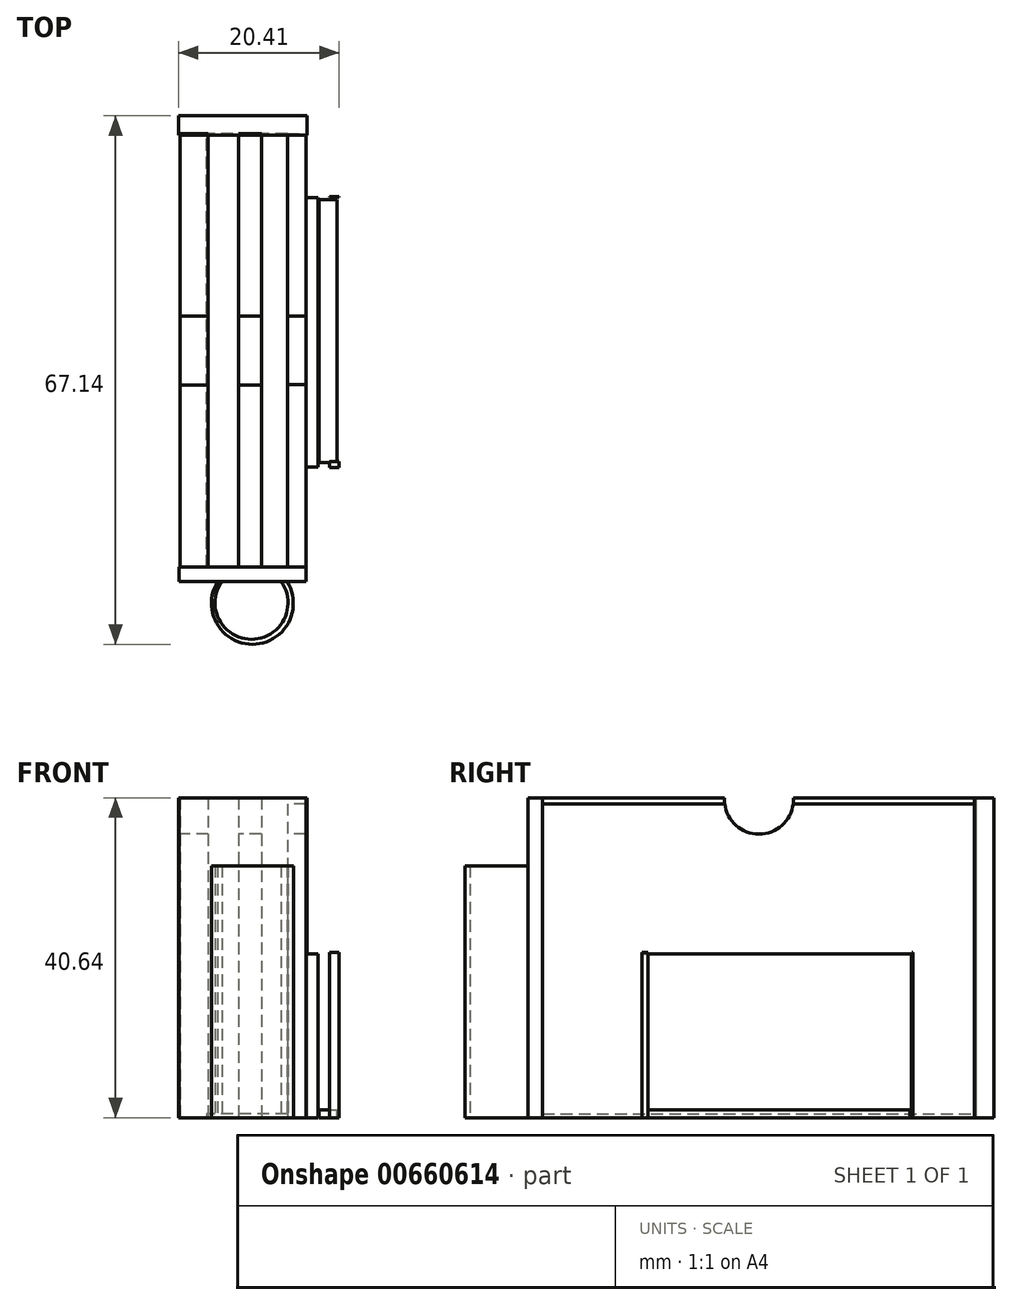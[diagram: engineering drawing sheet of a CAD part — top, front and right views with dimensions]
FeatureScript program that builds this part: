
annotation { "Feature Type Name" : "Feature", "Feature Type Description" : "" }
export const myFeature = defineFeature(function(context is Context, id is Id, definition is map)
    precondition{}
    {
        {
            var Q0;
            Q0=qCreatedBy(makeId("Top.planeOp"),FACE);
            var sketch = newSketch(context, id + "F0", { "sketchPlane" : qUnion([Q0])});
            skLineSegment(sketch, "E0.bottom", {"start": v(0, 0) * mm, "end": v(2.34, 0) * mm});
            skLineSegment(sketch, "E0.top", {"start": v(0, 55.03) * mm, "end": v(2.34, 55.03) * mm});
            skLineSegment(sketch, "E0.left", {"start": v(0, 0) * mm, "end": v(0, 55.03) * mm});
            skLineSegment(sketch, "E0.right", {"start": v(2.34, 0) * mm, "end": v(2.34, 55.03) * mm});
            skSolve(sketch);
        }
        {
            var Q0;
            Q0=makeQuery(id+"F0.imprint","IMPRINT",FACE,{"disambiguationData":[TD([[makeQuery(id+"F0.imprint","IMPRINT",EDGE,{"derivedFrom":sQuery(id+"F0.wireOp",EDGE,"E0.bottom")}),1.0]])]});
            extrude(context, id + "F1", {"entities" : qUnion([Q0]), "depth" : 39.88 * mm, "offsetDistance" : 25.4 * mm});
        }
        {
            var Q0;
            Q0=qCreatedBy(makeId("Top.planeOp"),FACE);
            var sketch = newSketch(context, id + "F2", { "sketchPlane" : qUnion([Q0])});
            skLineSegment(sketch, "E1", {"start": v(0, 0) * mm, "end": v(-3.29, 0) * mm});
            skLineSegment(sketch, "E2", {"start": v(-3.29, 0) * mm, "end": v(-3.29, 55.03) * mm});
            skLineSegment(sketch, "E3", {"start": v(-3.29, 55.03) * mm, "end": v(0, 55.03) * mm});
            skLineSegment(sketch, "E4", {"start": v(0, 55.03) * mm, "end": v(-6.23, 55.03) * mm});
            skLineSegment(sketch, "E5", {"start": v(-6.23, 55.03) * mm, "end": v(-6.23, 0) * mm});
            skLineSegment(sketch, "E6", {"start": v(-6.23, 0) * mm, "end": v(-3.29, 0) * mm});
            skLineSegment(sketch, "E7", {"start": v(-10.05, 0) * mm, "end": v(-10.05, 55.03) * mm});
            skLineSegment(sketch, "E8", {"start": v(-10.05, 55.03) * mm, "end": v(-6.23, 55.03) * mm});
            skLineSegment(sketch, "E9", {"start": v(-10.05, 0) * mm, "end": v(-6.23, 0) * mm});
            skLineSegment(sketch, "E10", {"start": v(-10.05, 55.03) * mm, "end": v(-13.63, 55.03) * mm});
            skLineSegment(sketch, "E11", {"start": v(-13.63, 55.03) * mm, "end": v(-13.63, 0) * mm});
            skLineSegment(sketch, "E12", {"start": v(-13.63, 0) * mm, "end": v(-10.05, 0) * mm});
            skSolve(sketch);
        }
        {
            var Q0;
            {var subQ0=sQuery(id+"F2.wireOp",EDGE,"E2");Q0=makeQuery(id+"F2.imprint","IMPRINT",FACE,{"disambiguationData":[TD([[makeQuery(id+"F2.imprint","IMPRINT",EDGE,{"derivedFrom":subQ0}),1.0]])]});}
            var Q1;
            Q1=makeQuery(id+"F2.imprint","IMPRINT",FACE,{"disambiguationData":[TD([[makeQuery(id+"F2.imprint","IMPRINT",EDGE,{"derivedFrom":sQuery(id+"F2.wireOp",EDGE,"E7")}),1.0]])]});
            extrude(context, id + "F3", {"entities" : qUnion([Q0, Q1]), "depth" : 40.64 * mm, "offsetDistance" : 25.4 * mm});
        }
        {
            var Q0;
            Q0=qCreatedBy(makeId("Top.planeOp"),FACE);
            var sketch = newSketch(context, id + "F4", { "sketchPlane" : qUnion([Q0])});
            skLineSegment(sketch, "E13", {"start": v(-13.78, 0) * mm, "end": v(2.4, 0) * mm});
            skLineSegment(sketch, "E14", {"start": v(2.4, 0) * mm, "end": v(2.4, -1.87) * mm});
            skLineSegment(sketch, "E15", {"start": v(2.4, -1.87) * mm, "end": v(-13.78, -1.87) * mm});
            skLineSegment(sketch, "E16", {"start": v(-13.78, -1.87) * mm, "end": v(-13.78, 0) * mm});
            skSolve(sketch);
        }
        {
            var Q0;
            Q0=makeQuery(id+"F4.imprint","IMPRINT",FACE,{"disambiguationData":[TD([[makeQuery(id+"F4.imprint","IMPRINT",EDGE,{"derivedFrom":sQuery(id+"F4.wireOp",EDGE,"E13")}),-1.0]])]});
            extrude(context, id + "F5", {"entities" : qUnion([Q0]), "depth" : 40.64 * mm, "offsetDistance" : 25.4 * mm});
        }
        {
            var Q0;
            Q0=qCreatedBy(makeId("Top.planeOp"),FACE);
            var sketch = newSketch(context, id + "F6", { "sketchPlane" : qUnion([Q0])});
            skLineSegment(sketch, "E17.bottom", {"start": v(2.5, 54.85) * mm, "end": v(-13.83, 54.85) * mm});
            skLineSegment(sketch, "E17.top", {"start": v(2.5, 57.3) * mm, "end": v(-13.83, 57.3) * mm});
            skLineSegment(sketch, "E17.left", {"start": v(2.5, 54.85) * mm, "end": v(2.5, 57.3) * mm});
            skLineSegment(sketch, "E17.right", {"start": v(-13.83, 54.85) * mm, "end": v(-13.83, 57.3) * mm});
            skSolve(sketch);
        }
        {
            var Q0;
            Q0=makeQuery(id+"F6.imprint","IMPRINT",FACE,{"disambiguationData":[TD([[makeQuery(id+"F6.imprint","IMPRINT",EDGE,{"derivedFrom":sQuery(id+"F6.wireOp",EDGE,"E17.bottom")}),-1.0]])]});
            extrude(context, id + "F7", {"entities" : qUnion([Q0]), "depth" : 40.64 * mm, "offsetDistance" : 25.4 * mm});
        }
        {
            var Q0;
            Q0=makeQuery(id+"F3.opExtrude","SWEPT_FACE",FACE,{"disambiguationData":[OSD([sQuery(id+"F2.wireOp",EDGE,"E11")])]});
            var sketch = newSketch(context, id + "F8", { "sketchPlane" : qUnion([Q0])});
            skArc(sketch, "E18", {"start": v(-31.86, 40.64) * mm, "mid": v(-27.5, 36.01) * mm, "end": v(-23.12, 40.64) * mm});
            skSolve(sketch);
        }
        {
            var Q0;
            {var subQ0=sQuery(id+"F8.wireOp",EDGE,"E18");Q0=makeQuery(id+"F8.imprint","IMPRINT",FACE,{"disambiguationData":[TD([[makeQuery(id+"F8.imprint","IMPRINT",EDGE,{"derivedFrom":subQ0}),1.0]])]});}
            extrude(context, id + "F9", {"entities" : qUnion([Q0]), "operationType" : NewBodyOperationType.REMOVE, "oppositeDirection" : true, "depth" : 1524 * mm, "offsetDistance" : 25.4 * mm});
        }
        {
            var Q0;
            Q0=qCreatedBy(makeId("Top.planeOp"),FACE);
            var sketch = newSketch(context, id + "F10", { "sketchPlane" : qUnion([Q0])});
            skLineSegment(sketch, "E19.bottom", {"start": v(0, 0) * mm, "end": v(-10.27, 0) * mm});
            skLineSegment(sketch, "E19.top", {"start": v(0, 55.02) * mm, "end": v(-10.27, 55.02) * mm});
            skLineSegment(sketch, "E19.left", {"start": v(0, 0) * mm, "end": v(0, 55.02) * mm});
            skLineSegment(sketch, "E19.right", {"start": v(-10.27, 0) * mm, "end": v(-10.27, 55.02) * mm});
            skSolve(sketch);
        }
        {
            var Q0;
            Q0 = qSketchRegion(id + "F10", true);
            extrude(context, id + "F11", {"entities" : qUnion([Q0]), "depth" : 0.5 * mm, "offsetDistance" : 25.4 * mm});
        }
        {
            var Q0;
            Q0=makeQuery(id+"F1.opExtrude","SWEPT_FACE",FACE,{"disambiguationData":[OSD([sQuery(id+"F0.wireOp",EDGE,"E0.right")])]});
            var sketch = newSketch(context, id + "F12", { "sketchPlane" : qUnion([Q0])});
            skLineSegment(sketch, "E20.bottom", {"start": v(12.7, 20.81) * mm, "end": v(46.89, 20.81) * mm});
            skLineSegment(sketch, "E20.top", {"start": v(12.7, 0) * mm, "end": v(46.89, 0) * mm});
            skLineSegment(sketch, "E20.left", {"start": v(12.7, 20.81) * mm, "end": v(12.7, 0) * mm});
            skLineSegment(sketch, "E20.right", {"start": v(46.89, 20.81) * mm, "end": v(46.89, 0) * mm});
            skSolve(sketch);
        }
        {
            var Q0;
            Q0=makeQuery(id+"F12.imprint","IMPRINT",FACE,{"disambiguationData":[TD([[makeQuery(id+"F12.imprint","IMPRINT",EDGE,{"derivedFrom":sQuery(id+"F12.wireOp",EDGE,"E20.bottom")}),-1.0]])]});
            extrude(context, id + "F13", {"entities" : qUnion([Q0]), "operationType" : NewBodyOperationType.ADD, "depth" : 1.52 * mm, "offsetDistance" : 25.4 * mm});
        }
        {
            var Q0;
            Q0=qCreatedBy(makeId("Top.planeOp"),FACE);
            var sketch = newSketch(context, id + "F14", { "sketchPlane" : qUnion([Q0])});
            skLineSegment(sketch, "E21.bottom", {"start": v(3.91, 12.62) * mm, "end": v(5.38, 12.62) * mm});
            skLineSegment(sketch, "E21.top", {"start": v(3.91, 46.95) * mm, "end": v(5.38, 46.95) * mm});
            skLineSegment(sketch, "E21.left", {"start": v(3.91, 12.62) * mm, "end": v(3.91, 46.95) * mm});
            skLineSegment(sketch, "E21.right", {"start": v(5.38, 12.62) * mm, "end": v(5.38, 46.95) * mm});
            skLineSegment(sketch, "E22.bottom", {"start": v(5.38, 12.62) * mm, "end": v(6.58, 12.62) * mm});
            skLineSegment(sketch, "E22.top", {"start": v(5.38, 47.04) * mm, "end": v(6.58, 47.04) * mm});
            skLineSegment(sketch, "E22.left", {"start": v(5.38, 12.62) * mm, "end": v(5.38, 47.04) * mm});
            skLineSegment(sketch, "E22.right", {"start": v(6.58, 12.62) * mm, "end": v(6.58, 47.04) * mm});
            skLineSegment(sketch, "E23.bottom", {"start": v(3.91, 12.62) * mm, "end": v(6.58, 12.62) * mm});
            skLineSegment(sketch, "E23.top", {"start": v(3.91, 13.37) * mm, "end": v(6.58, 13.37) * mm});
            skLineSegment(sketch, "E23.left", {"start": v(3.91, 12.62) * mm, "end": v(3.91, 13.37) * mm});
            skLineSegment(sketch, "E23.right", {"start": v(6.58, 12.62) * mm, "end": v(6.58, 13.37) * mm});
            skLineSegment(sketch, "E24.bottom", {"start": v(3.91, 46.95) * mm, "end": v(6.58, 46.95) * mm});
            skLineSegment(sketch, "E24.top", {"start": v(3.91, 46.2) * mm, "end": v(6.58, 46.2) * mm});
            skLineSegment(sketch, "E24.left", {"start": v(3.91, 46.95) * mm, "end": v(3.91, 46.2) * mm});
            skLineSegment(sketch, "E24.right", {"start": v(6.58, 46.95) * mm, "end": v(6.58, 46.2) * mm});
            skSolve(sketch);
        }
        {
            var Q0;
            {var subQ3=sQuery(id+"F14.wireOp",EDGE,"E22.bottom");Q0=makeQuery(id+"F14.imprint","IMPRINT",FACE,{"disambiguationData":[TD([[makeQuery(id+"F14.imprint","IMPRINT",EDGE,{"derivedFrom":subQ3}),1.0]])]});}
            var Q1;
            {var subQ0=sQuery(id+"F14.wireOp",EDGE,"E23.top");var subQ1=sQuery(id+"F14.wireOp",EDGE,"E22.left");var subQ2=makeQuery(id+"F14.imprint","INTERSECT",VERTEX,{"derivedFrom":[subQ1,subQ0]});Q1=makeQuery(id+"F14.imprint","IMPRINT",FACE,{"disambiguationData":[TD([[makeQuery(id+"F14.imprint","IMPRINT",EDGE,{"disambiguationData":[TD([[subQ2,-1.0]])],"derivedFrom":subQ1}),-1.0]])]});}
            var Q2;
            {var subQ5=sQuery(id+"F14.wireOp",EDGE,"E24.right");Q2=makeQuery(id+"F14.imprint","IMPRINT",FACE,{"disambiguationData":[TD([[makeQuery(id+"F14.imprint","IMPRINT",EDGE,{"derivedFrom":subQ5}),-1.0]])]});}
            var Q3;
            {var subQ5=sQuery(id+"F14.wireOp",EDGE,"E24.left");Q3=makeQuery(id+"F14.imprint","IMPRINT",FACE,{"disambiguationData":[TD([[makeQuery(id+"F14.imprint","IMPRINT",EDGE,{"derivedFrom":subQ5}),1.0]])]});}
            var Q4;
            {var subQ5=sQuery(id+"F14.wireOp",EDGE,"E23.right");Q4=makeQuery(id+"F14.imprint","IMPRINT",FACE,{"disambiguationData":[TD([[makeQuery(id+"F14.imprint","IMPRINT",EDGE,{"derivedFrom":subQ5}),1.0]])]});}
            var Q5;
            {var subQ5=sQuery(id+"F14.wireOp",EDGE,"E23.left");Q5=makeQuery(id+"F14.imprint","IMPRINT",FACE,{"disambiguationData":[TD([[makeQuery(id+"F14.imprint","IMPRINT",EDGE,{"derivedFrom":subQ5}),-1.0]])]});}
            extrude(context, id + "F15", {"entities" : qUnion([Q0, Q1, Q2, Q3, Q4, Q5]), "depth" : 20.98 * mm, "offsetDistance" : 25.4 * mm});
        }
        {
            var Q0;
            Q0=qCreatedBy(makeId("Top.planeOp"),FACE);
            var sketch = newSketch(context, id + "F16", { "sketchPlane" : qUnion([Q0])});
            skLineSegment(sketch, "E25.bottom", {"start": v(4, 13.25) * mm, "end": v(6.31, 13.25) * mm});
            skLineSegment(sketch, "E25.top", {"start": v(4, 46.67) * mm, "end": v(6.31, 46.67) * mm});
            skLineSegment(sketch, "E25.left", {"start": v(4, 13.25) * mm, "end": v(4, 46.67) * mm});
            skLineSegment(sketch, "E25.right", {"start": v(6.31, 13.25) * mm, "end": v(6.31, 46.67) * mm});
            skSolve(sketch);
        }
        {
            var Q0;
            Q0 = qSketchRegion(id + "F16", true);
            extrude(context, id + "F17", {"entities" : qUnion([Q0]), "operationType" : NewBodyOperationType.ADD, "depth" : 1.02 * mm, "offsetDistance" : 25.4 * mm});
        }
        {
            var Q0;
            Q0=qCreatedBy(makeId("Top.planeOp"),FACE);
            var sketch = newSketch(context, id + "F18", { "sketchPlane" : qUnion([Q0])});
            skArc(sketch, "E26", {"start": v(-8.2, -1.7) * mm, "mid": v(-4.46, -9.2) * mm, "end": v(-1.04, -1.55) * mm});
            skLineSegment(sketch, "E27", {"start": v(-8.2, -1.7) * mm, "end": v(-1.04, -1.55) * mm});
            skArc(sketch, "E28", {"start": v(-8.45, -1.32) * mm, "mid": v(-4.35, -9.83) * mm, "end": v(-0.56, -1.18) * mm});
            skLineSegment(sketch, "E29", {"start": v(-8.45, -1.32) * mm, "end": v(-0.56, -1.18) * mm});
            skSolve(sketch);
        }
        {
            var Q0;
            Q0 = qSketchRegion(id + "F18", true);
            extrude(context, id + "F19", {"entities" : qUnion([Q0]), "operationType" : NewBodyOperationType.ADD, "depth" : 32 * mm, "offsetDistance" : 25.4 * mm});
        }
    });
